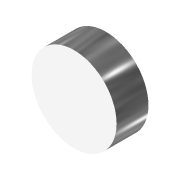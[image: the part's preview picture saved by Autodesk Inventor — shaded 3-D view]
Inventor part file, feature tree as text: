
AUTODESK INVENTOR PART (.ipt)
format: ipt  version: 2022 (Build 260153000, 153)  size: 80,896 bytes
history: native  units: mm
features: extrude x1, sketch x1
ambient origin geometry x8: Origin, YZ Plane, XZ Plane, XY Plane, X Axis, Y Axis, Z Axis, Center Point
bodies: Volumenkörper1 (feature_tree)
feature tree (2):
  extrude  "Extrusion1"  Depth=3.0mm TaperAngle=0.0deg
  sketch  "Skizze1"  dims[d0=8.0mm d1=3.0mm d2=0.0mm]
